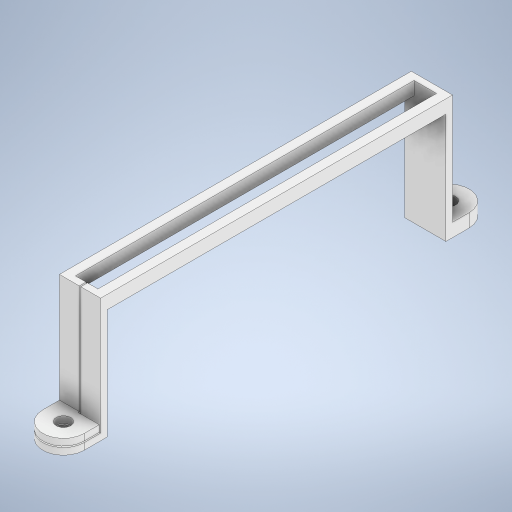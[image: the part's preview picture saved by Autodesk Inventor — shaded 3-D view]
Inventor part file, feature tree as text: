
AUTODESK INVENTOR PART (.ipt)
format: ipt  version: 2023 (Build 270158000, 158)  size: 334,848 bytes
history: native  units: mm
features: extrude x6, sketch x2, plane x1
ambient origin geometry x8: Origin, YZ Plane, XZ Plane, XY Plane, X Axis, Y Axis, Z Axis, Center Point
bodies: Solid1 (feature_tree)
feature tree (9):
  sketch  "Sketch1"  dims[d0=2.2mm d1=2.0mm]
  extrude  "Extrusion1"  Depth=2.0mm
  extrude  "Extrusion5"  Depth=2.0mm
  extrude  "Extrusion2"  Depth=58.0mm
  extrude  "Extrusion3"  Depth=0.2mm
  plane  "Work Plane3"
  extrude  "Extrusion6"  Depth=0.2mm
  extrude  "Extrusion8"  Depth=1.0mm
  sketch  "Sketch2"  dims[d2=2.2mm d3=2.0mm d4=58.0mm d5=3.5mm d6=3.5mm d7=1.0mm d8=1.0mm d9=2.0mm d10=0.0mm d11=16.6mm d12=0.0mm d13=1.4mm d14=1.4mm d15=2.0mm d16=0.0mm d17=0.1mm d24=1.0mm d25=0.0mm d26=0.2mm d28=0.1mm d29=1.0mm d30=0.2mm d31=1.0mm d32=0.0mm d35=1.0mm d36=0.0mm d37=0.2mm d38=0.1mm d33=0.872665mm]
